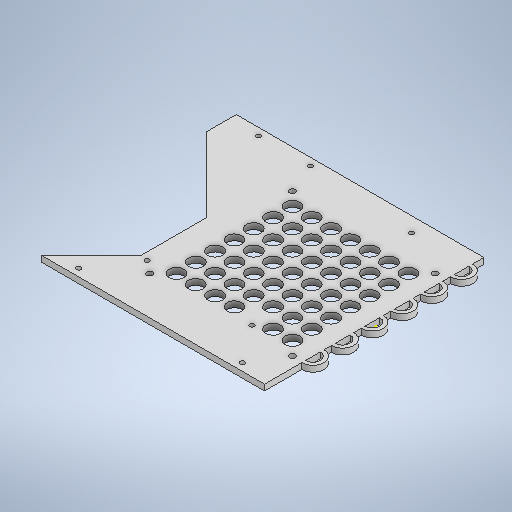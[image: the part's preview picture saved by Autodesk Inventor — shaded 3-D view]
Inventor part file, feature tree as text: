
AUTODESK INVENTOR PART (.ipt)
format: ipt  version: 2025.2 (Build 292293000, 293)  size: 887,296 bytes
history: native  units: in
note: dims shown in document units (in); Inventor stores cm internally (conversion verified against a paired STEP export)
features: sketch x9, extrude x6
ambient origin geometry x8: Origin, YZ Plane, XZ Plane, XY Plane, X Axis, Y Axis, Z Axis, Center Point
bodies: Solid1 (feature_tree)
feature tree (15):
  extrude  "Extrusion1"  Depth=0.1575in
  extrude  "Extrusion2"  Depth=0.1969in
  extrude  "Extrusion3"  Depth=0.126in
  extrude  "Extrusion4"  Depth=0.1969in
  extrude  "Extrusion5"  Depth=0.1181in
  sketch  "Sketch6"  dims[d15=0.1181in]
  extrude  "Extrusion6"  Depth=4.3307in
  sketch  "Sketch1"  dims[d0=0.1575in d1=0.0in d2=0.7874in]
  sketch  "Sketch2"  dims[d5=0.126in d6=0.126in]
  sketch  "Sketch3"  dims[d10=0.7874in d11=0.1181in]
  sketch  "Sketch4"  dims[d12=1.378in d13=4.3307in]
  sketch  "Sketch5"  dims[d14=0.1181in]
  sketch  "Sketch Rectangular Pattern1"  dims[d3=0.1969in d4=0.7874in]
  sketch  "Sketch7"  dims[d16=0.3937in d17=0.0in d18=1.5157in d19=1.1811in d20=4.2323in d21=0.1181in d22=0.1181in d23=0.3937in d24=0.0in d25=4.3307in d26=4.3307in d27=3.7795in d28=3.7795in d29=0.1575in d30=0.1575in d31=0.1575in d32=0.1575in d33=0.3937in d34=2.7559in d36=0.5118in d37=2.7559in d39=0.5118in d42=0.3937in d43=0.0in d44=0.5906in d45=0.3937in d46=0.5906in d47=2.3622in d49=0.7874in d50=0.3937in d52=0.3937in d54=0.3937in d55=0.0in]
  sketch  "Sketch Rectangular Pattern2"  dims[d7=0.3937in d8=0.0in d9=0.1969in]
